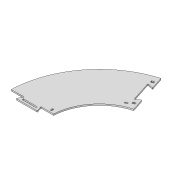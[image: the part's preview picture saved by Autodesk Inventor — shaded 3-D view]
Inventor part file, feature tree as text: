
AUTODESK INVENTOR PART (.ipt)
format: ipt  version: 2020 (Build 240168000, 168)  size: 309,248 bytes
history: native  units: mm
features: extrude x1, sketch x1
ambient origin geometry x8: Origin, YZ Plane, XZ Plane, XY Plane, X Axis, Y Axis, Z Axis, Center Point
bodies: Solid1 (feature_tree)
feature tree (2):
  extrude  "Extrusion1"  Depth=1.75mm
  sketch  "Sketch1"  dims[d0=504.787567mm d1=944.787567mm d2=50.0mm d4=360.0deg d6=7.5mm d7=7.5mm d9=68.5mm d10=7.5mm d11=7.5mm d12=3.5mm d13=3.5mm d17=50.0mm d19=360.0deg d21=4.363323mm d25=10.0mm d26=10.0mm d27=1.75mm d28=30.0mm d30=25.132741mm d32=271.25mm d33=7.5mm d34=13.5mm d36=1.75mm d40=20.0mm d44=7.0mm d45=0.0mm d46=0.0mm d47=8.0mm d48=1.75mm d50=50.0mm d52=50.0mm d54=30.0mm d62=50.0mm d64=50.0mm d66=30.0mm d67=1.75mm]
